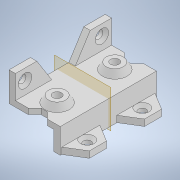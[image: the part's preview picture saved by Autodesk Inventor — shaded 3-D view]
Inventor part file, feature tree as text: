
AUTODESK INVENTOR PART (.ipt)
format: ipt  version: 2022 (Build 260153000, 153)  size: 236,032 bytes
history: native  units: mm
features: extrude x6, sketch x6, projected_geometry x5, hole x2, draft x2, plane x1
ambient origin geometry x8: Origin, YZ Plane, XZ Plane, XY Plane, X Axis, Y Axis, Z Axis, Center Point
bodies: Solid1 (feature_tree)
feature tree (22):
  extrude  "Extrusion1"  Depth=21.0mm
  extrude  "Extrusion2"  Depth=3.0mm
  plane  "Work Plane1"
  extrude  "Extrusion3"  Depth=11.0mm
  hole  "Hole1"  [1 undecoded]
  extrude  "Extrusion4"  TaperAngle=0.0deg  [1 undecoded]
  hole  "Hole2"  [1 undecoded]
  sketch  "Sketch7"  dims[d14=45.0deg d15=45.0deg d16=3.0mm d17=3.0mm d18=3.0mm d19=0.0mm d20=0.0mm d21=4.5mm d22=4.5mm d23=3.6mm d24=6.0mm d25=6.3mm d26=2.0mm d27=90.0deg d28=8.0mm d29=20.594885mm d30=8.0mm d31=8.0mm d32=8.0mm d33=8.0mm d34=4.0mm d35=4.0mm d36=3.0mm d37=0.0mm d38=11.0mm d39=3.6mm d40=6.0mm d41=6.3mm d42=2.0mm d43=90.0deg d44=8.0mm d45=20.594885mm d46=5.15mm d48=4.0mm d49=13.5mm d50=13.5mm d51=8.0mm d52=3.0mm d53=0.0mm d54=1.0mm d55=0.0mm d59=30.0deg d60=30.0deg d61=27.0mm d62=3.0mm]
  extrude  "Extrusion5"  Depth=3.0mm
  extrude  "Extrusion6"  Depth=3.0mm
  draft  "FaceDraft1"
  draft  "FaceDraft2"
  sketch  "Sketch1"  dims[d0=2.65mm d1=21.0mm]
  sketch  "Sketch2"  dims[d2=9.0mm d3=3.0mm]
  projected_geometry  "Projected Loop1"
  sketch  "Sketch3"  dims[d4=3.0mm d5=11.0mm]
  projected_geometry  "Projected Loop2"
  sketch  "Sketch4"  dims[d6=45.0mm d7=0.0mm d10=10.0mm]
  projected_geometry  "Projected Loop3"
  sketch  "Sketch6"  dims[d11=10.0mm d12=0.0mm d13=0.0mm]
  projected_geometry  "Projected Loop4"
  projected_geometry  "Projected Loop5"
note: 3 required parameter values undecoded (feature->parameter linkage not recoverable at this tier; creation-order binding heuristic only, values carry confidence <= 0.55)
